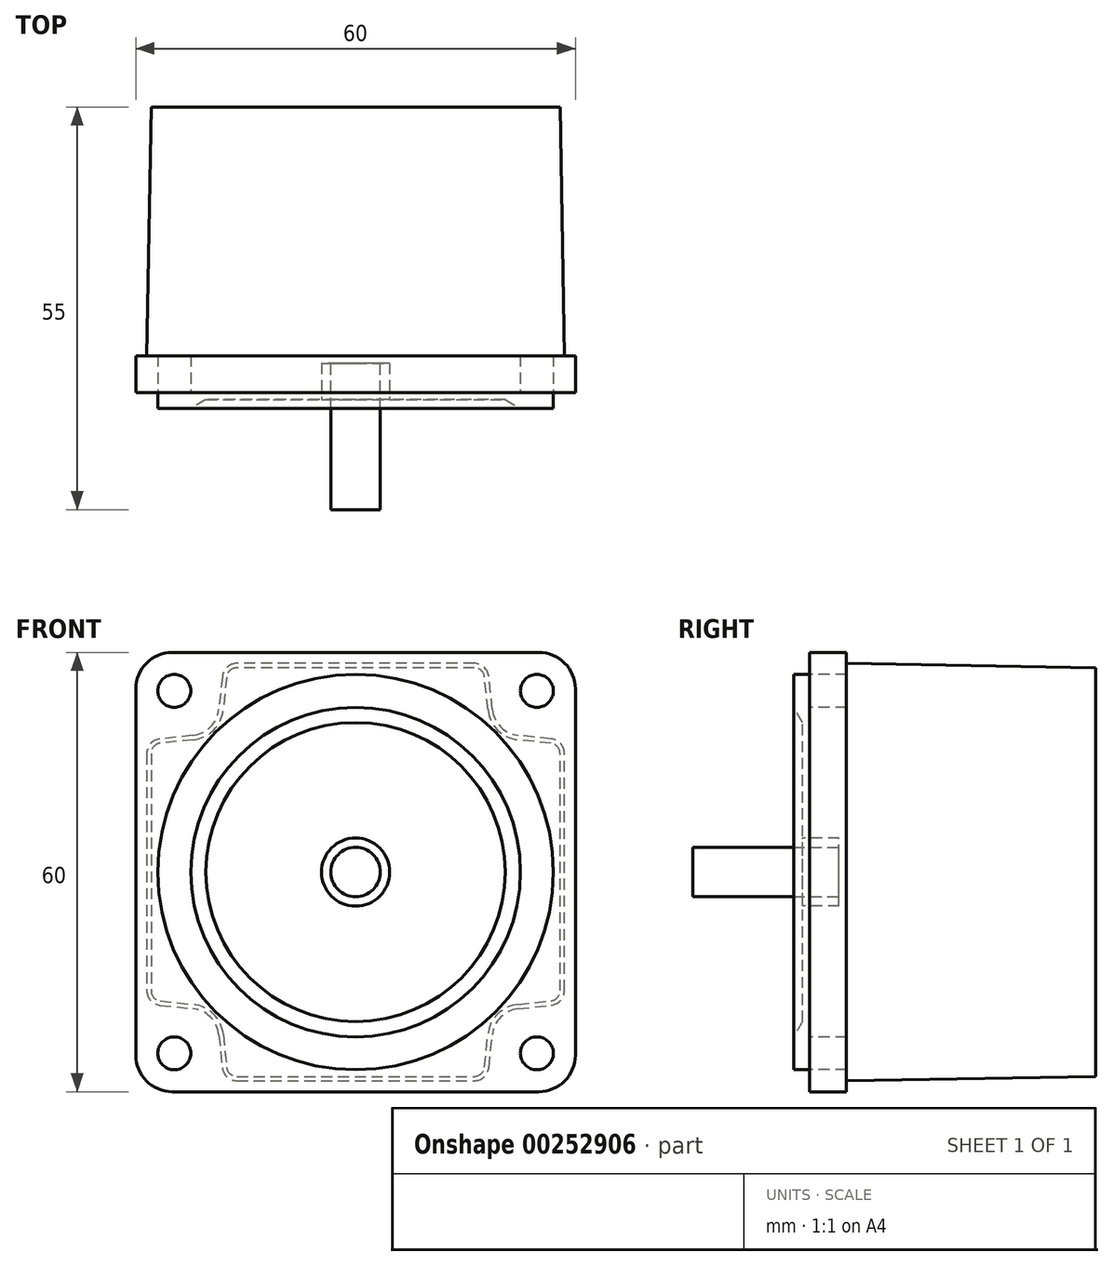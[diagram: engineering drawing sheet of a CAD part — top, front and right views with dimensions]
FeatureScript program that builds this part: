
annotation { "Feature Type Name" : "Feature", "Feature Type Description" : "" }
export const myFeature = defineFeature(function(context is Context, id is Id, definition is map)
    precondition{}
    {
        {
            var Q0;
            Q0=qCreatedBy(makeId("Front.planeOp"),FACE);
            var sketch = newSketch(context, id + "F0", { "sketchPlane" : qUnion([Q0])});
            skLineSegment(sketch, "E0.bottom", {"start": v(25, 30) * mm, "end": v(-25, 30) * mm});
            skLineSegment(sketch, "E0.top", {"start": v(25, -30) * mm, "end": v(-25, -30) * mm});
            skLineSegment(sketch, "E0.left", {"start": v(30, 25) * mm, "end": v(30, -25) * mm});
            skLineSegment(sketch, "E0.right", {"start": v(-30, 25) * mm, "end": v(-30, -25) * mm});
            skPoint(sketch, "E0.middle", {"position": v(0, 0) * mm});
            skPoint(sketch, "E1.visualSharp", {"position": v(-30, 30) * mm});
            skArc(sketch, "E1.filletArc", {"start": v(-25, 30) * mm, "mid": v(-28.54, 28.54) * mm, "end": v(-30, 25) * mm});
            skCircle(sketch, "E2", {"center": v(-24.75, 24.75) * mm, "radius": 2.25 * mm});
            skCircle(sketch, "E3.MirrorC", {"center": v(24.75, 24.75) * mm, "radius": 2.25 * mm});
            skCircle(sketch, "E4.MirrorC", {"center": v(-24.75, -24.75) * mm, "radius": 2.25 * mm});
            skCircle(sketch, "E5.MirrorC", {"center": v(24.75, -24.75) * mm, "radius": 2.25 * mm});
            skArc(sketch, "E6.MirrorCS", {"start": v(-25, -30) * mm, "mid": v(-28.54, -28.54) * mm, "end": v(-30, -25) * mm});
            skArc(sketch, "E7.MirrorCS", {"start": v(25, -30) * mm, "mid": v(28.54, -28.54) * mm, "end": v(30, -25) * mm});
            skArc(sketch, "E8.MirrorCS", {"start": v(25, 30) * mm, "mid": v(28.54, 28.54) * mm, "end": v(30, 25) * mm});
            skPoint(sketch, "E9.orphan", {"position": v(30, 30) * mm});
            skPoint(sketch, "E10.orphan", {"position": v(30, -30) * mm});
            skPoint(sketch, "E11.orphan", {"position": v(-30, -30) * mm});
            skSolve(sketch);
        }
        {
            var Q0;
            Q0 = qSketchRegion(id + "F0", true);
            extrude(context, id + "F1", {"entities" : qUnion([Q0]), "oppositeDirection" : true, "depth" : 5 * mm});
        }
        {
            var Q0;
            Q0=makeQuery(id+"F1.opExtrude","CAP_FACE",FACE,{"disambiguationData":[OSD([sQuery(id+"F0.wireOp",EDGE,"E0.bottom"),sQuery(id+"F0.wireOp",EDGE,"E0.top"),sQuery(id+"F0.wireOp",EDGE,"E0.left"),sQuery(id+"F0.wireOp",EDGE,"E0.right"),sQuery(id+"F0.wireOp",EDGE,"E1.filletArc"),sQuery(id+"F0.wireOp",EDGE,"E2"),sQuery(id+"F0.wireOp",EDGE,"E3.MirrorC"),sQuery(id+"F0.wireOp",EDGE,"E4.MirrorC"),sQuery(id+"F0.wireOp",EDGE,"E5.MirrorC"),sQuery(id+"F0.wireOp",EDGE,"E6.MirrorCS"),sQuery(id+"F0.wireOp",EDGE,"E7.MirrorCS"),sQuery(id+"F0.wireOp",EDGE,"E8.MirrorCS")])],"isStart":false});
            var sketch = newSketch(context, id + "F2", { "sketchPlane" : qUnion([Q0])});
            skLineSegment(sketch, "E12.top", {"start": v(16.2, -28.5) * mm, "end": v(-16.2, -28.5) * mm});
            skLineSegment(sketch, "E12.right", {"start": v(-28.5, 16.2) * mm, "end": v(-28.5, -16.2) * mm});
            skPoint(sketch, "E12.middle", {"position": v(0, 0) * mm});
            skLineSegment(sketch, "E13", {"start": v(-26.7, 18.19) * mm, "end": v(-22.22, 18.66) * mm});
            skLineSegment(sketch, "E14", {"start": v(-18.66, 22.22) * mm, "end": v(-18.19, 26.7) * mm});
            skLineSegment(sketch, "E15.MirrorCS", {"start": v(18.66, 22.22) * mm, "end": v(18.19, 26.7) * mm});
            skLineSegment(sketch, "E16.MirrorCS", {"start": v(26.7, 18.19) * mm, "end": v(22.22, 18.66) * mm});
            skLineSegment(sketch, "E17.MirrorCS", {"start": v(-26.7, -18.19) * mm, "end": v(-22.22, -18.66) * mm});
            skLineSegment(sketch, "E18.MirrorCS", {"start": v(-18.66, -22.22) * mm, "end": v(-18.19, -26.7) * mm});
            skLineSegment(sketch, "E19.MirrorCS", {"start": v(18.66, -22.22) * mm, "end": v(18.19, -26.7) * mm});
            skLineSegment(sketch, "E20.MirrorCS", {"start": v(26.7, -18.19) * mm, "end": v(22.22, -18.66) * mm});
            skPoint(sketch, "E21.newPointA", {"position": v(-28.5, 28.5) * mm});
            skPoint(sketch, "E21.newPointB", {"position": v(-28.5, 18) * mm});
            skArc(sketch, "E21.filletArc", {"start": v(-26.7, 18.19) * mm, "mid": v(-27.99, 17.54) * mm, "end": v(-28.5, 16.2) * mm});
            skPoint(sketch, "E22.newPointA", {"position": v(-18, 28.5) * mm});
            skArc(sketch, "E22.filletArc", {"start": v(-16.2, 28.5) * mm, "mid": v(-17.54, 27.99) * mm, "end": v(-18.19, 26.7) * mm});
            skPoint(sketch, "E23.visualSharp", {"position": v(-19, 19) * mm});
            skArc(sketch, "E23.filletArc", {"start": v(-22.22, 18.66) * mm, "mid": v(-19.81, 19.81) * mm, "end": v(-18.66, 22.22) * mm});
            skArc(sketch, "E24.MirrorCS", {"start": v(16.2, 28.5) * mm, "mid": v(17.54, 27.99) * mm, "end": v(18.19, 26.7) * mm});
            skArc(sketch, "E25.MirrorCS", {"start": v(22.22, 18.66) * mm, "mid": v(19.81, 19.81) * mm, "end": v(18.66, 22.22) * mm});
            skArc(sketch, "E26.MirrorCS", {"start": v(26.7, 18.19) * mm, "mid": v(27.99, 17.54) * mm, "end": v(28.5, 16.2) * mm});
            skArc(sketch, "E27.MirrorCS", {"start": v(-26.7, -18.19) * mm, "mid": v(-27.99, -17.54) * mm, "end": v(-28.5, -16.2) * mm});
            skArc(sketch, "E28.MirrorCS", {"start": v(-22.22, -18.66) * mm, "mid": v(-19.81, -19.81) * mm, "end": v(-18.66, -22.22) * mm});
            skArc(sketch, "E29.MirrorCS", {"start": v(-16.2, -28.5) * mm, "mid": v(-17.54, -27.99) * mm, "end": v(-18.19, -26.7) * mm});
            skArc(sketch, "E30.MirrorCS", {"start": v(16.2, -28.5) * mm, "mid": v(17.54, -27.99) * mm, "end": v(18.19, -26.7) * mm});
            skArc(sketch, "E31.MirrorCS", {"start": v(22.22, -18.66) * mm, "mid": v(19.81, -19.81) * mm, "end": v(18.66, -22.22) * mm});
            skArc(sketch, "E32.MirrorCS", {"start": v(26.7, -18.19) * mm, "mid": v(27.99, -17.54) * mm, "end": v(28.5, -16.2) * mm});
            skPoint(sketch, "E33.orphan", {"position": v(19, 19) * mm});
            skPoint(sketch, "E34.orphan", {"position": v(18, 28.5) * mm});
            skLineSegment(sketch, "E35.trimOffspring", {"start": v(16.2, 28.5) * mm, "end": v(-16.2, 28.5) * mm});
            skPoint(sketch, "E36.orphan", {"position": v(28.5, 18) * mm});
            skLineSegment(sketch, "E37.trimOffspring", {"start": v(28.5, 16.2) * mm, "end": v(28.5, -16.2) * mm});
            skPoint(sketch, "E12.bottom.start.orphan", {"position": v(28.5, 28.5) * mm});
            skPoint(sketch, "E38.orphan", {"position": v(19, -19) * mm});
            skPoint(sketch, "E39.orphan", {"position": v(28.5, -18) * mm});
            skPoint(sketch, "E40.orphan", {"position": v(28.5, -28.5) * mm});
            skPoint(sketch, "E41.orphan", {"position": v(18, -28.5) * mm});
            skPoint(sketch, "E42.orphan", {"position": v(-18, -28.5) * mm});
            skPoint(sketch, "E43.orphan", {"position": v(-19, -19) * mm});
            skPoint(sketch, "E44.orphan", {"position": v(-28.5, -28.5) * mm});
            skPoint(sketch, "E45.orphan", {"position": v(-28.5, -18) * mm});
            skSolve(sketch);
        }
        {
            var Q0;
            Q0 = qSketchRegion(id + "F2", true);
            extrude(context, id + "F3", {"entities" : qUnion([Q0]), "operationType" : NewBodyOperationType.ADD, "depth" : 34 * mm, "hasDraft" : true, "draftAngle" : 1 * degree, "draftPullDirection" : true});
        }
        {
            var Q0;
            Q0=makeQuery(id+"F1.opExtrude","CAP_FACE",FACE,{"disambiguationData":[OSD([sQuery(id+"F0.wireOp",EDGE,"E0.bottom"),sQuery(id+"F0.wireOp",EDGE,"E0.top"),sQuery(id+"F0.wireOp",EDGE,"E0.left"),sQuery(id+"F0.wireOp",EDGE,"E0.right"),sQuery(id+"F0.wireOp",EDGE,"E1.filletArc"),sQuery(id+"F0.wireOp",EDGE,"E2"),sQuery(id+"F0.wireOp",EDGE,"E3.MirrorC"),sQuery(id+"F0.wireOp",EDGE,"E4.MirrorC"),sQuery(id+"F0.wireOp",EDGE,"E5.MirrorC"),sQuery(id+"F0.wireOp",EDGE,"E6.MirrorCS"),sQuery(id+"F0.wireOp",EDGE,"E7.MirrorCS"),sQuery(id+"F0.wireOp",EDGE,"E8.MirrorCS")])],"isStart":true});
            var sketch = newSketch(context, id + "F4", { "sketchPlane" : qUnion([Q0])});
            skCircle(sketch, "E46", {"center": v(0, 0) * mm, "radius": 27 * mm});
            skSolve(sketch);
        }
        {
            var Q0;
            Q0 = qSketchRegion(id + "F4", true);
            extrude(context, id + "F5", {"entities" : qUnion([Q0]), "operationType" : NewBodyOperationType.ADD, "depth" : 2.2 * mm});
        }
        {
            var Q0;
            Q0=makeQuery(id+"F5.opExtrude","CAP_FACE",FACE,{"disambiguationData":[OSD([sQuery(id+"F4.wireOp",EDGE,"E46")])],"isStart":false});
            var sketch = newSketch(context, id + "F6", { "sketchPlane" : qUnion([Q0])});
            skCircle(sketch, "E47", {"center": v(0, 0) * mm, "radius": 22.5 * mm});
            skSolve(sketch);
        }
        {
            var Q0;
            Q0 = qSketchRegion(id + "F6", true);
            extrude(context, id + "F7", {"entities" : qUnion([Q0]), "operationType" : NewBodyOperationType.REMOVE, "oppositeDirection" : true, "depth" : 1.2 * mm, "hasDraft" : true, "draftAngle" : 60 * degree, "draftPullDirection" : true});
        }
        {
            var Q0;
            Q0=makeQuery(id+"F7.boolean.opBoolean","COPY",FACE,{"derivedFrom":makeQuery(id+"F7.opExtrude","CAP_FACE",FACE,{"disambiguationData":[OSD([sQuery(id+"F6.wireOp",EDGE,"E47")])],"isStart":false})});
            var sketch = newSketch(context, id + "F8", { "sketchPlane" : qUnion([Q0])});
            skCircle(sketch, "E48", {"center": v(0, 0) * mm, "radius": 4.65 * mm});
            skSolve(sketch);
        }
        {
            var Q0;
            Q0 = qSketchRegion(id + "F8", true);
            extrude(context, id + "F9", {"entities" : qUnion([Q0]), "operationType" : NewBodyOperationType.REMOVE, "oppositeDirection" : true, "depth" : 5 * mm});
        }
        {
            var Q0;
            Q0=makeQuery(id+"F9.boolean.opBoolean","COPY",FACE,{"derivedFrom":makeQuery(id+"F9.opExtrude","CAP_FACE",FACE,{"disambiguationData":[OSD([sQuery(id+"F8.wireOp",EDGE,"E48")])],"isStart":false})});
            var sketch = newSketch(context, id + "F10", { "sketchPlane" : qUnion([Q0])});
            skCircle(sketch, "E49", {"center": v(0, 0) * mm, "radius": 3.38 * mm});
            skSolve(sketch);
        }
        {
            var Q0;
            Q0 = qSketchRegion(id + "F10", true);
            extrude(context, id + "F11", {"entities" : qUnion([Q0]), "operationType" : NewBodyOperationType.ADD, "depth" : 20 * mm});
        }
    });
